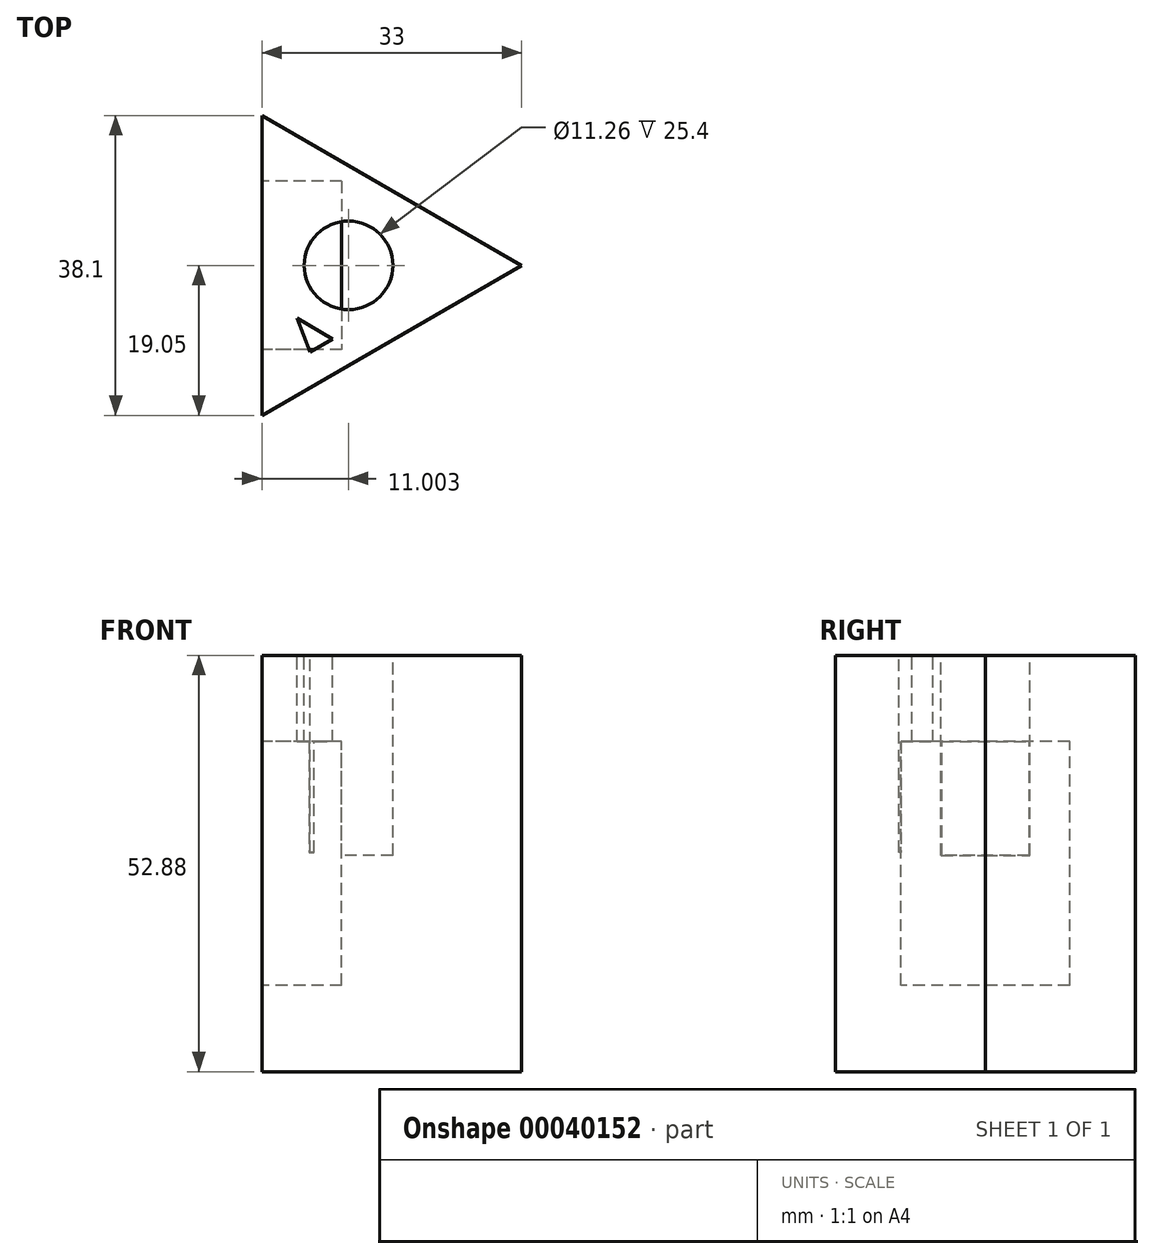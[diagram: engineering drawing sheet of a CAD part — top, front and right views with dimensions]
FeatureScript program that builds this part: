
annotation { "Feature Type Name" : "Feature", "Feature Type Description" : "" }
export const myFeature = defineFeature(function(context is Context, id is Id, definition is map)
    precondition{}
    {
        {
            var Q0;
            Q0=qCreatedBy(makeId("Top.planeOp"),FACE);
            var sketch = newSketch(context, id + "F0", { "sketchPlane" : qUnion([Q0])});
            skLineSegment(sketch, "E0", {"start": v(0, 0) * mm, "end": v(-33, -19.05) * mm});
            skLineSegment(sketch, "E1", {"start": v(-33, -19.05) * mm, "end": v(-33, 19.05) * mm});
            skLineSegment(sketch, "E2", {"start": v(-33, 19.05) * mm, "end": v(0, 0) * mm});
            skSolve(sketch);
        }
        {
            var Q0;
            Q0 = qSketchRegion(id + "F0", true);
            extrude(context, id + "F1", {"entities" : qUnion([Q0]), "depth" : 52.88 * mm});
        }
        {
            var Q0;
            Q0=makeQuery(id+"F1.opExtrude","CAP_FACE",FACE,{"disambiguationData":[OSD([sQuery(id+"F0.wireOp",EDGE,"E0"),sQuery(id+"F0.wireOp",EDGE,"E1"),sQuery(id+"F0.wireOp",EDGE,"E2")])],"isStart":false});
            var sketch = newSketch(context, id + "F2", { "sketchPlane" : qUnion([Q0])});
            skCircle(sketch, "E3", {"center": v(-22, 0) * mm, "radius": 5.63 * mm});
            skLineSegment(sketch, "E4", {"start": v(0, 0) * mm, "end": v(-33, 0) * mm, "construction": true});
            skLineSegment(sketch, "E5", {"start": v(-16.5, 9.52) * mm, "end": v(-33, -19.05) * mm, "construction": true});
            skLineSegment(sketch, "E6", {"start": v(-16.5, -9.53) * mm, "end": v(-33, 19.05) * mm, "construction": true});
            skSolve(sketch);
        }
        {
            var Q0;
            Q0 = qSketchRegion(id + "F2", true);
            extrude(context, id + "F3", {"entities" : qUnion([Q0]), "operationType" : NewBodyOperationType.REMOVE, "oppositeDirection" : true, "depth" : 25.4 * mm});
        }
        {
            var Q0;
            Q0=makeQuery(id+"F1.opExtrude","SWEPT_FACE",FACE,{"disambiguationData":[OSD([sQuery(id+"F0.wireOp",EDGE,"E1")])]});
            var sketch = newSketch(context, id + "F4", { "sketchPlane" : qUnion([Q0])});
            skLineSegment(sketch, "E7.bottom", {"start": v(-10.7, 10.96) * mm, "end": v(10.7, 10.96) * mm});
            skLineSegment(sketch, "E7.top", {"start": v(-10.7, 41.92) * mm, "end": v(10.7, 41.92) * mm});
            skLineSegment(sketch, "E7.left", {"start": v(-10.7, 10.96) * mm, "end": v(-10.7, 41.92) * mm});
            skLineSegment(sketch, "E7.right", {"start": v(10.7, 10.96) * mm, "end": v(10.7, 41.92) * mm});
            skLineSegment(sketch, "E8", {"start": v(-19.05, 26.44) * mm, "end": v(-10.7, 26.44) * mm, "construction": true});
            skLineSegment(sketch, "E9", {"start": v(10.7, 26.44) * mm, "end": v(19.05, 26.44) * mm, "construction": true});
            skLineSegment(sketch, "E10", {"start": v(0, 10.96) * mm, "end": v(0, 0) * mm, "construction": true});
            skLineSegment(sketch, "E11", {"start": v(0, 41.92) * mm, "end": v(0, 52.88) * mm, "construction": true});
            skSolve(sketch);
        }
        {
            var Q0;
            Q0 = qSketchRegion(id + "F4", true);
            extrude(context, id + "F5", {"entities" : qUnion([Q0]), "operationType" : NewBodyOperationType.REMOVE, "oppositeDirection" : true, "depth" : 10.13 * mm});
        }
        {
            var Q0;
            Q0=makeQuery(id+"F1.opExtrude","CAP_FACE",FACE,{"disambiguationData":[OSD([sQuery(id+"F0.wireOp",EDGE,"E0"),sQuery(id+"F0.wireOp",EDGE,"E1"),sQuery(id+"F0.wireOp",EDGE,"E2")])],"isStart":false});
            var sketch = newSketch(context, id + "F6", { "sketchPlane" : qUnion([Q0])});
            skLineSegment(sketch, "E12", {"start": v(-28.52, -6.7) * mm, "end": v(-26.91, -11) * mm});
            skLineSegment(sketch, "E13", {"start": v(-26.91, -11) * mm, "end": v(-24.03, -9.36) * mm});
            skLineSegment(sketch, "E14", {"start": v(-24.03, -9.36) * mm, "end": v(-28.52, -6.7) * mm});
            skSolve(sketch);
        }
        {
            var Q0;
            Q0 = qSketchRegion(id + "F6", true);
            extrude(context, id + "F7", {"entities" : qUnion([Q0]), "operationType" : NewBodyOperationType.REMOVE, "oppositeDirection" : true, "depth" : 25 * mm});
        }
    });
